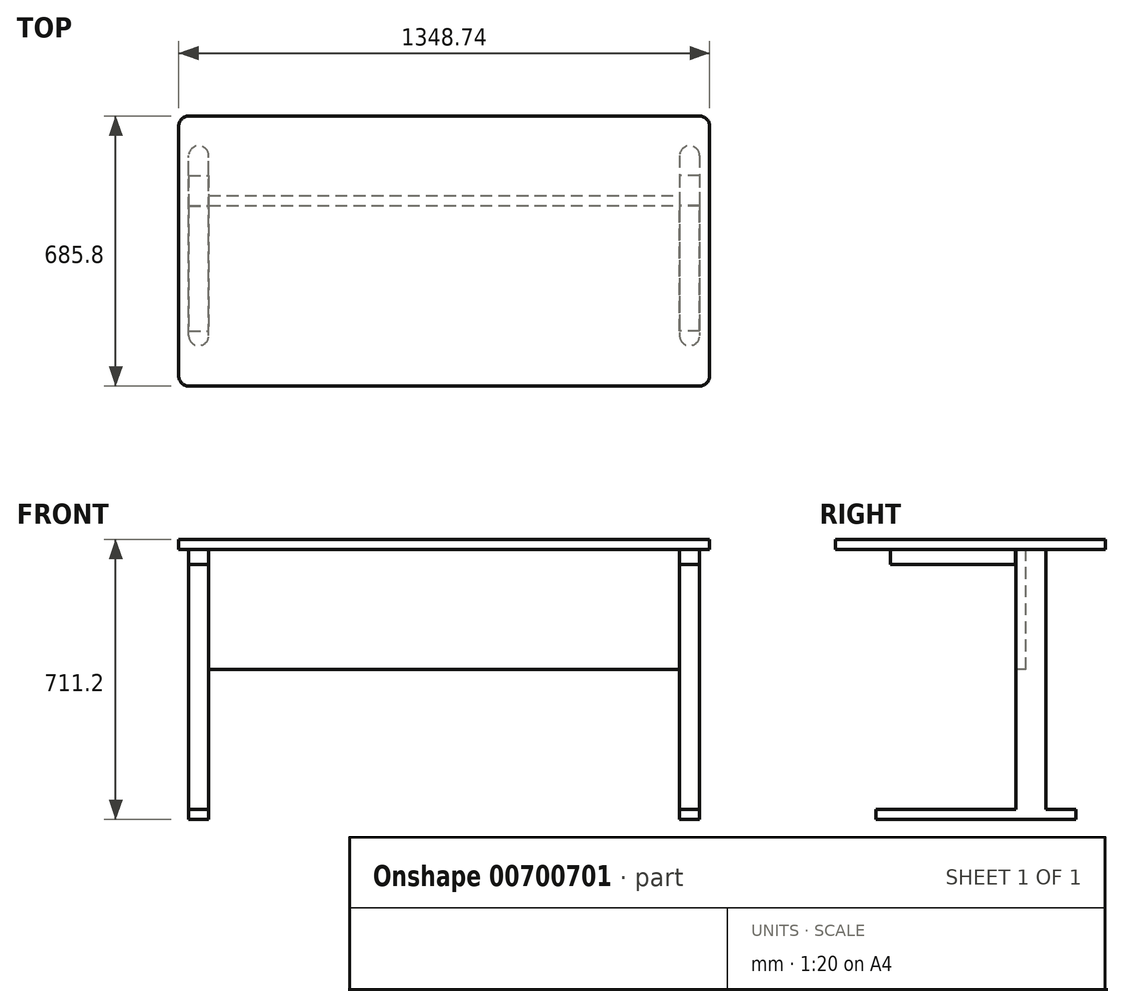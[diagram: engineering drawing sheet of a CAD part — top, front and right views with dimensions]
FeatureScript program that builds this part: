
annotation { "Feature Type Name" : "Feature", "Feature Type Description" : "" }
export const myFeature = defineFeature(function(context is Context, id is Id, definition is map)
    precondition{}
    {
        {
            var Q0;
            Q0=qCreatedBy(makeId("Top.planeOp"),FACE);
            var sketch = newSketch(context, id + "F0", { "sketchPlane" : qUnion([Q0])});
            skLineSegment(sketch, "E0.bottom", {"start": v(648.97, -342.9) * mm, "end": v(-648.97, -342.9) * mm});
            skLineSegment(sketch, "E0.top", {"start": v(648.97, 342.9) * mm, "end": v(-648.97, 342.9) * mm});
            skLineSegment(sketch, "E0.left", {"start": v(674.37, -317.5) * mm, "end": v(674.37, 317.5) * mm});
            skLineSegment(sketch, "E0.right", {"start": v(-674.37, -317.5) * mm, "end": v(-674.37, 317.5) * mm});
            skPoint(sketch, "E0.middle", {"position": v(0, 0) * mm});
            skPoint(sketch, "E1.visualSharp", {"position": v(-674.37, 342.9) * mm});
            skArc(sketch, "E1.filletArc", {"start": v(-648.97, 342.9) * mm, "mid": v(-666.93, 335.46) * mm, "end": v(-674.37, 317.5) * mm});
            skPoint(sketch, "E2.visualSharp", {"position": v(674.37, 342.9) * mm});
            skArc(sketch, "E2.filletArc", {"start": v(674.37, 317.5) * mm, "mid": v(666.93, 335.46) * mm, "end": v(648.97, 342.9) * mm});
            skPoint(sketch, "E3.visualSharp", {"position": v(674.37, -342.9) * mm});
            skArc(sketch, "E3.filletArc", {"start": v(648.97, -342.9) * mm, "mid": v(666.93, -335.46) * mm, "end": v(674.37, -317.5) * mm});
            skPoint(sketch, "E4.visualSharp", {"position": v(-674.37, -342.9) * mm});
            skArc(sketch, "E4.filletArc", {"start": v(-674.37, -317.5) * mm, "mid": v(-666.93, -335.46) * mm, "end": v(-648.97, -342.9) * mm});
            skSolve(sketch);
        }
        {
            var Q0;
            Q0=makeQuery(id+"F0.imprint","IMPRINT",FACE,{"disambiguationData":[TD([[makeQuery(id+"F0.imprint","IMPRINT",EDGE,{"derivedFrom":sQuery(id+"F0.wireOp",EDGE,"E0.bottom")}),-1.0]])]});
            extrude(context, id + "F1", {"entities" : qUnion([Q0]), "endBound" : BoundingType.SYMMETRIC, "depth" : 25.4 * mm, "offsetDistance" : 25.4 * mm});
        }
        {
            var Q0;
            Q0=makeQuery(id+"F1.opExtrude","CAP_FACE",FACE,{"disambiguationData":[OSD([sQuery(id+"F0.wireOp",EDGE,"E0.bottom"),sQuery(id+"F0.wireOp",EDGE,"E0.top"),sQuery(id+"F0.wireOp",EDGE,"E0.left"),sQuery(id+"F0.wireOp",EDGE,"E0.right"),sQuery(id+"F0.wireOp",EDGE,"E1.filletArc"),sQuery(id+"F0.wireOp",EDGE,"E2.filletArc"),sQuery(id+"F0.wireOp",EDGE,"E3.filletArc"),sQuery(id+"F0.wireOp",EDGE,"E4.filletArc")])],"isStart":true});
            var sketch = newSketch(context, id + "F2", { "sketchPlane" : qUnion([Q0])});
            skSolve(sketch);
        }
        {
            var Q0;
            Q0=makeQuery(id+"F2.imprint","IMPRINT",FACE,{"disambiguationData":[TD([[makeQuery(id+"F2.imprint","IMPRINT",EDGE,{"derivedFrom":makeQuery(id+"F1.opExtrude","CAP_EDGE",EDGE,{"disambiguationData":[OSD([sQuery(id+"F0.wireOp",EDGE,"E0.bottom")])],"isStart":true})}),1.0]])]});
            var sketch = newSketch(context, id + "F3", { "sketchPlane" : qUnion([Q0])});
            skLineSegment(sketch, "E5.bottom", {"start": v(-648.97, -114.3) * mm, "end": v(-598.17, -114.3) * mm});
            skLineSegment(sketch, "E5.top", {"start": v(-648.97, 203.2) * mm, "end": v(-598.17, 203.2) * mm});
            skLineSegment(sketch, "E5.left", {"start": v(-648.97, -114.3) * mm, "end": v(-648.97, 203.2) * mm});
            skLineSegment(sketch, "E5.right", {"start": v(-598.17, -114.3) * mm, "end": v(-598.17, 203.2) * mm});
            skLineSegment(sketch, "E6.left", {"start": v(-648.97, 203.2) * mm, "end": v(-648.97, -114.3) * mm});
            skLineSegment(sketch, "E6.right", {"start": v(-598.17, 203.2) * mm, "end": v(-598.17, -114.3) * mm});
            skLineSegment(sketch, "E7.MirrorCS", {"start": v(598.17, 203.2) * mm, "end": v(598.17, -114.3) * mm});
            skLineSegment(sketch, "E8.MirrorCS", {"start": v(648.97, 203.2) * mm, "end": v(598.17, 203.2) * mm});
            skLineSegment(sketch, "E9.MirrorCS", {"start": v(648.97, 203.2) * mm, "end": v(648.97, -114.3) * mm});
            skLineSegment(sketch, "E10.MirrorCS", {"start": v(648.97, -114.3) * mm, "end": v(598.17, -114.3) * mm});
            skSolve(sketch);
        }
        {
            var Q0;
            Q0 = qSketchRegion(id + "F3", true);
            extrude(context, id + "F4", {"entities" : qUnion([Q0]), "depth" : 38.1 * mm, "offsetDistance" : 25.4 * mm});
        }
        {
            var Q0;
            Q0=makeQuery(id+"F2.imprint","IMPRINT",FACE,{"disambiguationData":[TD([[makeQuery(id+"F2.imprint","IMPRINT",EDGE,{"derivedFrom":makeQuery(id+"F1.opExtrude","CAP_EDGE",EDGE,{"disambiguationData":[OSD([sQuery(id+"F0.wireOp",EDGE,"E0.bottom")])],"isStart":true})}),1.0]])]});
            var sketch = newSketch(context, id + "F5", { "sketchPlane" : qUnion([Q0])});
            skLineSegment(sketch, "E11.bottom", {"start": v(-648.97, -191.3) * mm, "end": v(-598.17, -191.3) * mm});
            skLineSegment(sketch, "E11.top", {"start": v(-648.97, -115.1) * mm, "end": v(-598.17, -115.1) * mm});
            skLineSegment(sketch, "E11.left", {"start": v(-648.97, -191.3) * mm, "end": v(-648.97, -115.1) * mm});
            skLineSegment(sketch, "E11.right", {"start": v(-598.17, -191.3) * mm, "end": v(-598.17, -115.1) * mm});
            skLineSegment(sketch, "E12.MirrorCS", {"start": v(648.97, -191.3) * mm, "end": v(648.97, -115.1) * mm});
            skLineSegment(sketch, "E13.MirrorCS", {"start": v(648.97, -191.3) * mm, "end": v(598.17, -191.3) * mm});
            skLineSegment(sketch, "E14.MirrorCS", {"start": v(598.17, -191.3) * mm, "end": v(598.17, -115.1) * mm});
            skLineSegment(sketch, "E15.MirrorCS", {"start": v(648.97, -115.1) * mm, "end": v(598.17, -115.1) * mm});
            skSolve(sketch);
        }
        {
            var Q0;
            Q0 = qSketchRegion(id + "F5", true);
            extrude(context, id + "F6", {"entities" : qUnion([Q0]), "operationType" : NewBodyOperationType.ADD, "depth" : 660.4 * mm, "offsetDistance" : 25.4 * mm});
        }
        {
            var Q0;
            Q0=makeQuery(id+"F6.opExtrude","CAP_FACE",FACE,{"disambiguationData":[OSD([sQuery(id+"F5.wireOp",EDGE,"E11.bottom"),sQuery(id+"F5.wireOp",EDGE,"E11.top"),sQuery(id+"F5.wireOp",EDGE,"E11.left"),sQuery(id+"F5.wireOp",EDGE,"E11.right")])],"isStart":false});
            var sketch = newSketch(context, id + "F7", { "sketchPlane" : qUnion([Q0])});
            skLineSegment(sketch, "E16.bottom", {"start": v(-648.97, -191.3) * mm, "end": v(-598.17, -191.3) * mm});
            skLineSegment(sketch, "E16.top", {"start": v(-648.97, -242.1) * mm, "end": v(-598.17, -242.1) * mm});
            skLineSegment(sketch, "E16.left", {"start": v(-648.97, -191.3) * mm, "end": v(-648.97, -242.1) * mm});
            skLineSegment(sketch, "E16.right", {"start": v(-598.17, -191.3) * mm, "end": v(-598.17, -242.1) * mm});
            skArc(sketch, "E17", {"start": v(-648.97, -242.1) * mm, "mid": v(-623.57, -267.5) * mm, "end": v(-598.17, -242.1) * mm});
            skLineSegment(sketch, "E18.top", {"start": v(-648.97, 215.1) * mm, "end": v(-598.17, 215.1) * mm});
            skLineSegment(sketch, "E18.left", {"start": v(-648.97, -191.3) * mm, "end": v(-648.97, 215.1) * mm});
            skLineSegment(sketch, "E18.right", {"start": v(-598.17, -191.3) * mm, "end": v(-598.17, 215.1) * mm});
            skArc(sketch, "E19", {"start": v(-648.97, 215.1) * mm, "mid": v(-623.57, 240.5) * mm, "end": v(-598.17, 215.1) * mm});
            skLineSegment(sketch, "E20", {"start": v(0, 351.19) * mm, "end": v(0, -349.42) * mm});
            skArc(sketch, "E21.MirrorCS", {"start": v(648.97, 215.1) * mm, "mid": v(623.57, 240.5) * mm, "end": v(598.17, 215.1) * mm});
            skLineSegment(sketch, "E22.MirrorCS", {"start": v(598.17, -191.3) * mm, "end": v(598.17, 215.1) * mm});
            skLineSegment(sketch, "E23.MirrorCS", {"start": v(648.97, -191.3) * mm, "end": v(648.97, 215.1) * mm});
            skLineSegment(sketch, "E24.MirrorCS", {"start": v(648.97, -191.3) * mm, "end": v(648.97, -242.1) * mm});
            skLineSegment(sketch, "E25.MirrorCS", {"start": v(598.17, -191.3) * mm, "end": v(598.17, -242.1) * mm});
            skArc(sketch, "E26.MirrorCS", {"start": v(648.97, -242.1) * mm, "mid": v(623.57, -267.5) * mm, "end": v(598.17, -242.1) * mm});
            skLineSegment(sketch, "E27.MirrorCS", {"start": v(648.97, 215.1) * mm, "end": v(598.17, 215.1) * mm});
            skLineSegment(sketch, "E28.MirrorCS", {"start": v(648.97, -242.1) * mm, "end": v(598.17, -242.1) * mm});
            skSolve(sketch);
        }
        {
            var Q0;
            Q0 = qSketchRegion(id + "F7", true);
            extrude(context, id + "F8", {"entities" : qUnion([Q0]), "operationType" : NewBodyOperationType.ADD, "depth" : 25.4 * mm, "offsetDistance" : 25.4 * mm});
        }
        {
            var Q0;
            Q0=makeQuery(id+"F2.imprint","IMPRINT",FACE,{"disambiguationData":[TD([[makeQuery(id+"F2.imprint","IMPRINT",EDGE,{"derivedFrom":makeQuery(id+"F1.opExtrude","CAP_EDGE",EDGE,{"disambiguationData":[OSD([sQuery(id+"F0.wireOp",EDGE,"E0.bottom")])],"isStart":true})}),1.0]])]});
            var sketch = newSketch(context, id + "F9", { "sketchPlane" : qUnion([Q0])});
            skLineSegment(sketch, "E29.bottom", {"start": v(-648.46, -115.21) * mm, "end": v(646.94, -115.21) * mm});
            skLineSegment(sketch, "E29.top", {"start": v(-648.46, -140.61) * mm, "end": v(646.94, -140.61) * mm});
            skLineSegment(sketch, "E29.left", {"start": v(-648.46, -115.21) * mm, "end": v(-648.46, -140.61) * mm});
            skLineSegment(sketch, "E29.right", {"start": v(646.94, -115.21) * mm, "end": v(646.94, -140.61) * mm});
            skSolve(sketch);
        }
        {
            var Q0;
            Q0 = qSketchRegion(id + "F9", true);
            extrude(context, id + "F10", {"entities" : qUnion([Q0]), "operationType" : NewBodyOperationType.ADD, "depth" : 304.8 * mm, "offsetDistance" : 25.4 * mm});
        }
    });
